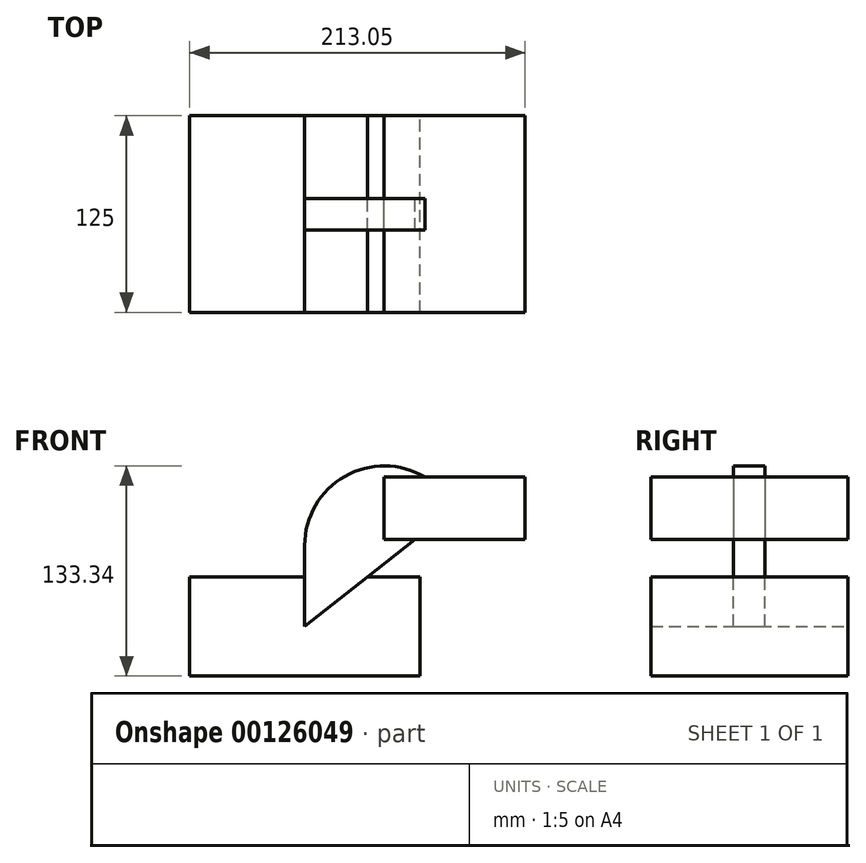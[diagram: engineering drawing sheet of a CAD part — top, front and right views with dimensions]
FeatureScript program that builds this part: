
annotation { "Feature Type Name" : "Feature", "Feature Type Description" : "" }
export const myFeature = defineFeature(function(context is Context, id is Id, definition is map)
    precondition{}
    {
        {
            var Q0;
            Q0=qCreatedBy(makeId("Front.planeOp"),FACE);
            var sketch = newSketch(context, id + "F0", { "sketchPlane" : qUnion([Q0])});
            skLineSegment(sketch, "E0.bottom", {"start": v(-73.1, 31.43) * mm, "end": v(73.1, 31.43) * mm});
            skLineSegment(sketch, "E0.top", {"start": v(-73.1, -31.43) * mm, "end": v(73.1, -31.43) * mm});
            skLineSegment(sketch, "E0.left", {"start": v(-73.1, 31.43) * mm, "end": v(-73.1, -31.43) * mm});
            skLineSegment(sketch, "E0.right", {"start": v(73.1, 31.43) * mm, "end": v(73.1, -31.43) * mm});
            skPoint(sketch, "E0.middle", {"position": v(0, 0) * mm});
            skLineSegment(sketch, "E1.bottom", {"start": v(139.95, 94.82) * mm, "end": v(50.27, 94.82) * mm});
            skLineSegment(sketch, "E1.top", {"start": v(139.95, 55.28) * mm, "end": v(50.27, 55.28) * mm});
            skLineSegment(sketch, "E1.left", {"start": v(139.95, 94.82) * mm, "end": v(139.95, 55.28) * mm});
            skLineSegment(sketch, "E1.right", {"start": v(50.27, 94.82) * mm, "end": v(50.27, 55.28) * mm});
            skPoint(sketch, "E1.middle", {"position": v(95.1, 75.05) * mm});
            skLineSegment(sketch, "E2", {"start": v(0, 0) * mm, "end": v(0, 51.43) * mm});
            skArc(sketch, "E3", {"start": v(0, 51.43) * mm, "mid": v(38.32, 100.43) * mm, "end": v(95.1, 75.05) * mm});
            skFitSpline(sketch, "E4", {"points": [v(0, 0) * mm, v(95.1, 75.05) * mm], "startDerivative": vector(95.1, 75.05) * mm, "endDerivative": vector(95.1, 75.05) * mm});
            skSolve(sketch);
        }
        {
            var Q0;
            Q0=makeQuery(id+"F0.imprint","IMPRINT",FACE,{"disambiguationData":[TD([[makeQuery(id+"F0.imprint","IMPRINT",EDGE,{"derivedFrom":sQuery(id+"F0.wireOp",EDGE,"E0.top")}),1.0]])]});
            var Q1;
            Q1=makeQuery(id+"F0.imprint","IMPRINT",FACE,{"disambiguationData":[TD([[makeQuery(id+"F0.imprint","IMPRINT",EDGE,{"derivedFrom":sQuery(id+"F0.wireOp",EDGE,"E1.top")}),-1.0]])]});
            extrude(context, id + "F1", {"entities" : qUnion([Q0, Q1]), "endBound" : BoundingType.SYMMETRIC, "depth" : 125 * mm});
        }
        {
            var Q0;
            {var subQ0=sQuery(id+"F0.wireOp",EDGE,"E1.right");Q0=makeQuery(id+"F0.imprint","IMPRINT",FACE,{"disambiguationData":[TD([[makeQuery(id+"F0.imprint","IMPRINT",EDGE,{"derivedFrom":subQ0}),-1.0]])]});}
            var Q1;
            {var subQ0=sQuery(id+"F0.wireOp",EDGE,"E2");var subQ1=sQuery(id+"F0.wireOp",EDGE,"E0.bottom");var subQ2=makeQuery(id+"F0.imprint","INTERSECT",VERTEX,{"derivedFrom":[subQ1,subQ0]});Q1=makeQuery(id+"F0.imprint","IMPRINT",FACE,{"disambiguationData":[TD([[makeQuery(id+"F0.imprint","IMPRINT",EDGE,{"disambiguationData":[TD([[subQ2,-1.0]])],"derivedFrom":subQ1}),-1.0]])]});}
            extrude(context, id + "F2", {"entities" : qUnion([Q0, Q1]), "endBound" : BoundingType.SYMMETRIC, "depth" : 20 * mm});
        }
    });
